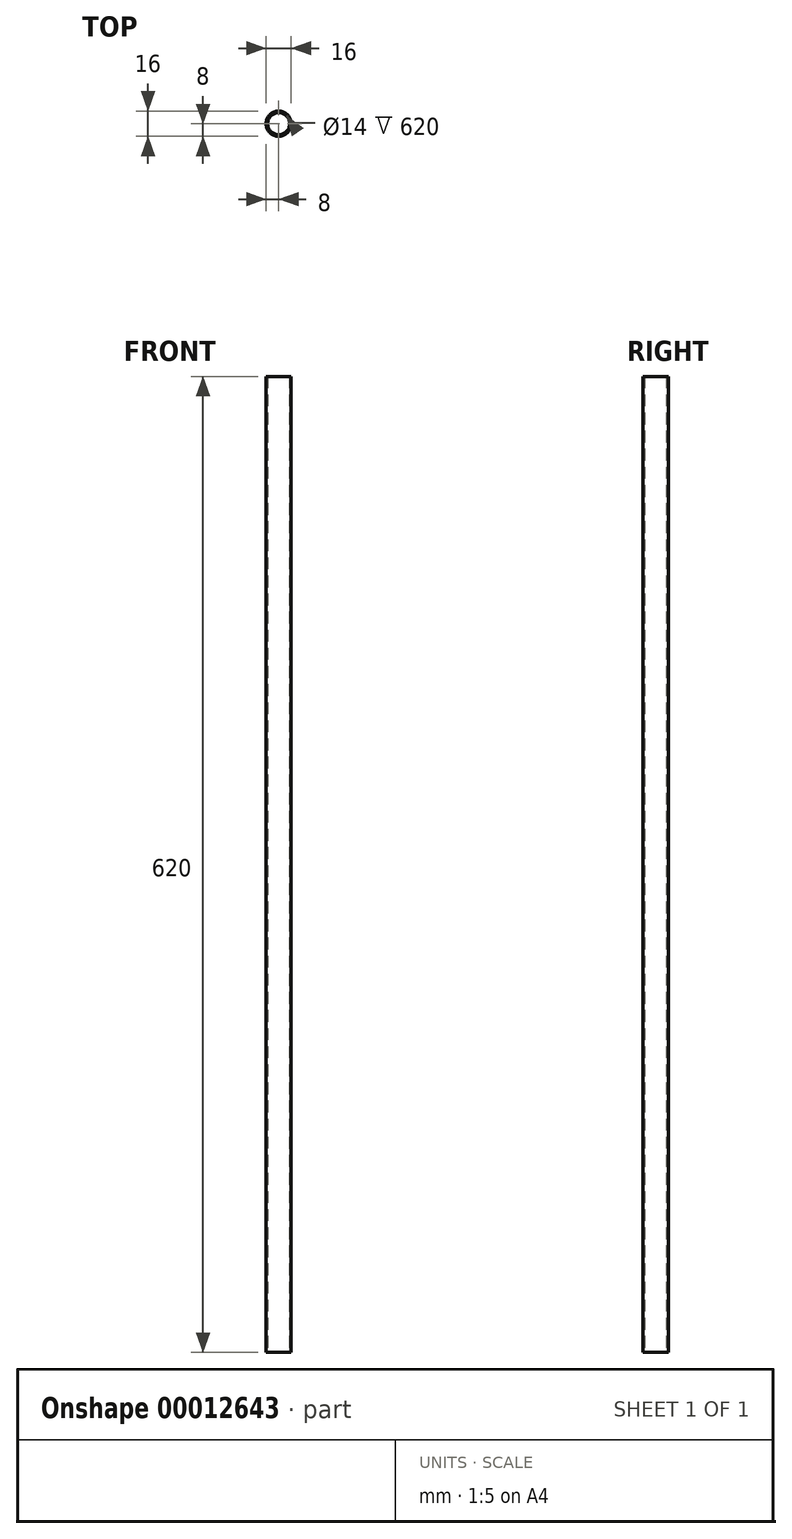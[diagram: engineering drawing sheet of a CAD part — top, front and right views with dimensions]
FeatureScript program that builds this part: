
annotation { "Feature Type Name" : "Feature", "Feature Type Description" : "" }
export const myFeature = defineFeature(function(context is Context, id is Id, definition is map)
    precondition{}
    {
        {
            var Q0;
            Q0=qCreatedBy(makeId("Top.planeOp"),FACE);
            var sketch = newSketch(context, id + "F0", { "sketchPlane" : qUnion([Q0])});
            skCircle(sketch, "E0", {"center": v(0, 0) * mm, "radius": 8 * mm});
            skCircle(sketch, "E1.0", {"center": v(0, 0) * mm, "radius": 7 * mm});
            skSolve(sketch);
        }
        {
            var Q0;
            Q0 = qSketchRegion(id + "F0", true);
            extrude(context, id + "F1", {"entities" : qUnion([Q0]), "depth" : 620 * mm});
        }
    });
